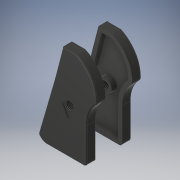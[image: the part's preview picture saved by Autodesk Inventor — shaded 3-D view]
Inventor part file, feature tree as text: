
AUTODESK INVENTOR PART (.ipt)
format: ipt  version: 2018 (Build 220112000, 112)  size: 719,872 bytes
history: native  units: in
note: dims shown in document units (in); Inventor stores cm internally (conversion verified against a paired STEP export)
features: extrude x6, sketch x6, fillet x4, projected_geometry x2, thread x1, plane x1, mirror x1
ambient origin geometry x8: Origin, YZ Plane, XZ Plane, XY Plane, X Axis, Y Axis, Z Axis, Center Point
bodies: Solid1 (feature_tree)
feature tree (21):
  extrude  "Extrusion1"  Depth=2.7165in
  extrude  "Extrusion2"  Depth=0.2756in TaperAngle=0.0deg
  extrude  "Extrusion7"  [1 undecoded]
  fillet  "Fillet11"  Radius=0.1969in
  fillet  "Fillet12"  Radius=0.1969in
  thread  "Thread2"  [1 undecoded]
  fillet  "Fillet14"  Radius=0.3543in
  extrude  "Extrusion10"  Depth=0.0394in
  fillet  "Fillet15"  Radius=0.0787in
  extrude  "Extrusion15"  Depth=0.0787in
  plane  "Work Plane1"
  mirror  "Mirror1"
  extrude  "Extrusion14"  Depth=0.1181in
  sketch  "Sketch1"  dims[d0=1.7717in d1=2.7165in]
  sketch  "Sketch2"  dims[d7=0.2756in d8=0.0in d14=0.0591in d15=0.0in]
  sketch  "Sketch8"  dims[d19=0.2362in d72=-0.3937in]
  sketch  "Sketch12"  dims[d101=7.874in d103=0.3937in d105=7.874in d107=0.3937in d109=7.874in d111=0.3937in d113=7.874in d115=0.3937in d117=7.874in d119=0.3937in d121=7.874in d123=0.3937in d125=7.874in d127=0.3937in d129=7.874in d131=0.3937in d173=0.1969in d174=0.1969in d175=0.3543in d176=0.3543in]
  projected_geometry  "Projected Loop5"
  sketch  "Sketch13"  dims[d177=0.0315in d178=0.0in d185=0.0394in d186=0.0787in]
  sketch  "Sketch14"  dims[d188=0.3937in d189=0.0in d191=0.0787in d195=0.1181in d196=0.0787in d197=0.1565in d198=0.0in d199=0.0394in d846=0.0472in d847=0.0in d903=0.0394in d904=0.0394in d905=0.0394in d906=0.0394in d907=0.0394in d908=0.0394in d909=0.0394in d910=0.0394in d911=0.0394in d912=0.0394in d913=0.0394in d914=0.0394in d915=0.0394in d916=0.0394in d932=0.0394in d933=0.0394in d934=0.0394in d935=0.0394in d936=0.0394in d937=0.0394in d938=0.0394in d939=0.0394in d940=0.0394in d941=0.0394in d942=0.0394in d943=0.0394in d944=0.0394in d945=0.0394in d946=0.0394in d948=0.0394in d954=0.0394in d958=0.0394in d959=0.0394in d960=0.0039in d961=0.0in]
  projected_geometry  "Projected Loop8"
note: 2 required parameter values undecoded (feature->parameter linkage not recoverable at this tier; creation-order binding heuristic only, values carry confidence <= 0.55)
